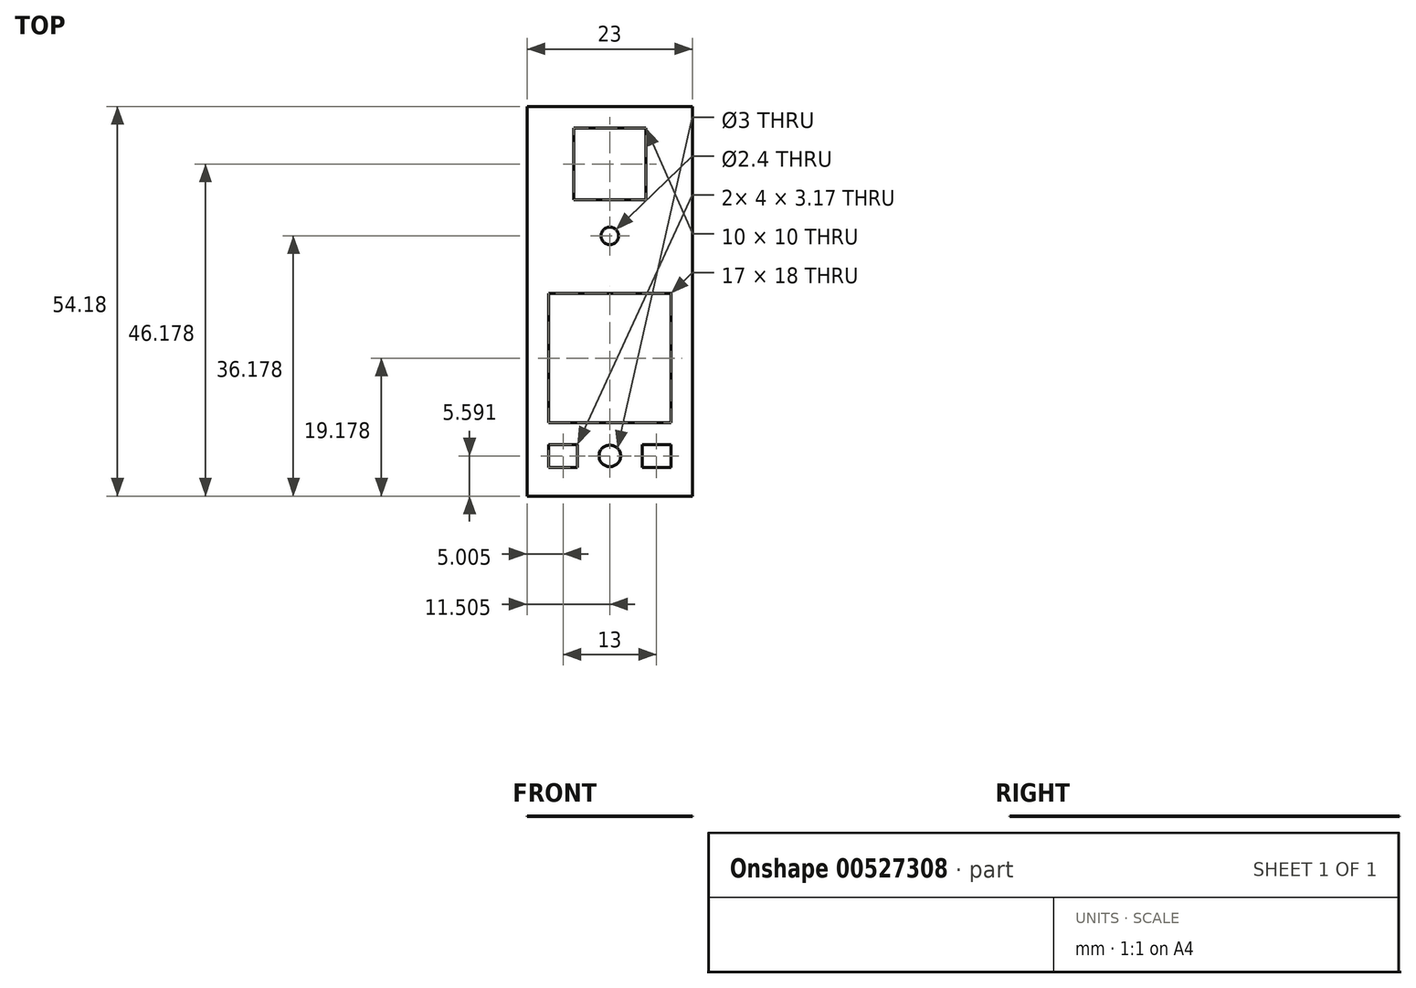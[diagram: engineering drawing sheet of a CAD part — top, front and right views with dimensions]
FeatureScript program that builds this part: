
annotation { "Feature Type Name" : "Feature", "Feature Type Description" : "" }
export const myFeature = defineFeature(function(context is Context, id is Id, definition is map)
    precondition{}
    {
        {
            var Q0;
            Q0=qCreatedBy(makeId("Top.planeOp"),FACE);
            var sketch = newSketch(context, id + "F0", { "sketchPlane" : qUnion([Q0])});
            skLineSegment(sketch, "E0.bottom", {"start": v(-0.08, -1.79) * mm, "end": v(22.92, -1.79) * mm});
            skLineSegment(sketch, "E0.top", {"start": v(-0.08, 52.39) * mm, "end": v(22.92, 52.39) * mm});
            skLineSegment(sketch, "E0.left", {"start": v(-0.08, -1.79) * mm, "end": v(-0.08, 52.39) * mm});
            skLineSegment(sketch, "E0.right", {"start": v(22.92, -1.79) * mm, "end": v(22.92, 52.39) * mm});
            skLineSegment(sketch, "E1.bottom", {"start": v(6.42, 39.39) * mm, "end": v(16.42, 39.39) * mm});
            skLineSegment(sketch, "E1.top", {"start": v(6.42, 29.39) * mm, "end": v(16.42, 29.39) * mm});
            skLineSegment(sketch, "E1.left", {"start": v(6.42, 39.39) * mm, "end": v(6.42, 29.39) * mm});
            skLineSegment(sketch, "E1.right", {"start": v(16.42, 39.39) * mm, "end": v(16.42, 29.39) * mm});
            skPoint(sketch, "E1.middle", {"position": v(11.42, 34.39) * mm});
            skLineSegment(sketch, "E2.top", {"start": v(6.42, 49.39) * mm, "end": v(16.42, 49.39) * mm});
            skLineSegment(sketch, "E2.left", {"start": v(6.42, 39.39) * mm, "end": v(6.42, 49.39) * mm});
            skLineSegment(sketch, "E2.right", {"start": v(16.42, 39.39) * mm, "end": v(16.42, 49.39) * mm});
            skCircle(sketch, "E3", {"center": v(11.42, 34.39) * mm, "radius": 1.2 * mm});
            skCircle(sketch, "E4", {"center": v(11.42, 3.8) * mm, "radius": 1.5 * mm});
            skLineSegment(sketch, "E5.bottom", {"start": v(2.92, 5.39) * mm, "end": v(6.92, 5.39) * mm});
            skLineSegment(sketch, "E5.top", {"start": v(2.92, 2.21) * mm, "end": v(6.92, 2.21) * mm});
            skLineSegment(sketch, "E5.left", {"start": v(2.92, 5.39) * mm, "end": v(2.92, 2.21) * mm});
            skLineSegment(sketch, "E5.right", {"start": v(6.92, 5.39) * mm, "end": v(6.92, 2.21) * mm});
            skPoint(sketch, "E5.middle", {"position": v(4.92, 3.8) * mm});
            skLineSegment(sketch, "E6", {"start": v(11.42, 3.8) * mm, "end": v(11.42, 5.3) * mm});
            skLineSegment(sketch, "E7.MirrorCS", {"start": v(15.92, 5.39) * mm, "end": v(15.92, 2.21) * mm});
            skLineSegment(sketch, "E8.MirrorCS", {"start": v(19.92, 5.39) * mm, "end": v(15.92, 5.39) * mm});
            skLineSegment(sketch, "E9.MirrorCS", {"start": v(19.92, 5.39) * mm, "end": v(19.92, 2.21) * mm});
            skLineSegment(sketch, "E10.MirrorCS", {"start": v(19.92, 2.21) * mm, "end": v(15.92, 2.21) * mm});
            skLineSegment(sketch, "E11.bottom", {"start": v(2.92, 8.39) * mm, "end": v(19.92, 8.39) * mm});
            skLineSegment(sketch, "E11.top", {"start": v(2.92, 26.39) * mm, "end": v(19.92, 26.39) * mm});
            skLineSegment(sketch, "E11.left", {"start": v(2.92, 8.39) * mm, "end": v(2.92, 26.39) * mm});
            skLineSegment(sketch, "E11.right", {"start": v(19.92, 8.39) * mm, "end": v(19.92, 26.39) * mm});
            skSolve(sketch);
        }
        {
            var Q0;
            {var subQ3=sQuery(id+"F0.wireOp",EDGE,"wtiJx0A3-Piaz-BVb3-eG2h-1XG7ABVZoibs.bottom");Q0=makeQuery(id+"F0.imprint","IMPRINT",FACE,{"disambiguationData":[TD([[makeQuery(id+"F0.imprint","IMPRINT",EDGE,{"derivedFrom":subQ3}),1.0]])]});}
            var Q1;
            Q1=makeQuery(id+"F0.imprint","IMPRINT",FACE,{"disambiguationData":[TD([[makeQuery(id+"F0.imprint","IMPRINT",EDGE,{"derivedFrom":sQuery(id+"F0.wireOp",EDGE,"E1.top")}),1.0]])]});
            var Q2;
            Q2=makeQuery(id+"F0.imprint","IMPRINT",FACE,{"disambiguationData":[TD([[makeQuery(id+"F0.imprint","IMPRINT",EDGE,{"derivedFrom":sQuery(id+"F0.wireOp",EDGE,"E0.bottom")}),1.0]])]});
            extrude(context, id + "F1", {"entities" : qUnion([Q0, Q1, Q2]), "depth" : 1 / 203.2 * mm, "offsetDistance" : 25 * mm});
        }
    });
